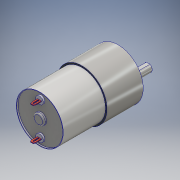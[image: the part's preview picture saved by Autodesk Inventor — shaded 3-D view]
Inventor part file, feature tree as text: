
AUTODESK INVENTOR PART (.ipt)
format: ipt  version: 2016 (Build 200138000, 138)  size: 331,776 bytes
history: native  units: mm
features: extrude x13, sketch x13, chamfer x6, fillet x1, projected_geometry x1
ambient origin geometry x8: Origin, YZ Plane, XZ Plane, XY Plane, X Axis, Y Axis, Z Axis, Center Point
bodies: Solid1 (feature_tree)
feature tree (34):
  extrude  "Extrusion1"  Depth=26.6mm TaperAngle=0.0deg
  extrude  "Extrusion2"  Depth=7.0mm
  chamfer  "Chamfer1"  Distance=6.5mm
  extrude  "Extrusion3"  TaperAngle=0.0deg  [1 undecoded]
  chamfer  "Chamfer3"  Distance=1.0mm
  extrude  "Extrusion4"  Depth=6.0mm
  extrude  "Extrusion5"  Depth=4.3mm
  extrude  "Extrusion6"  Depth=12.0mm
  sketch  "Sketch7"  dims[d16=22.8mm d17=1.0mm d18=0.0mm]
  extrude  "Extrusion7"  Depth=33.8mm
  extrude  "Extrusion8"  Depth=1.0mm
  fillet  "Fillet1"  Radius=2.0mm
  extrude  "Extrusion9"  Depth=12.0mm
  extrude  "Extrusion10"  TaperAngle=0.0deg  [1 undecoded]
  extrude  "Extrusion11"  Depth=12.0mm
  chamfer  "Chamfer4"  Distance=20.0mm Angle=360.0deg
  chamfer  "Chamfer5"  Distance=1.2mm
  extrude  "Extrusion12"  Depth=12.0mm
  chamfer  "Chamfer6"  [1 undecoded]
  chamfer  "Chamfer7"  Distance=3.0mm
  extrude  "Extrusion13"  Depth=12.0mm
  sketch  "Sketch1"  dims[d0=36.8mm d3=26.6mm d4=0.0mm]
  sketch  "Sketch2"  dims[d5=0.0mm d6=7.0mm]
  sketch  "Sketch3"  dims[d7=12.0mm d8=6.5mm d9=0.0mm]
  projected_geometry  "Projected Loop1"
  sketch  "Sketch4"  dims[d10=0.5mm d11=2.0mm d12=45.0deg d13=0.0mm]
  sketch  "Sketch5"  dims[d14=7.0mm]
  sketch  "Sketch6"  dims[d15=17.0mm]
  sketch  "Sketch10"  dims[d22=1.0mm d23=2.0mm d24=45.0deg d25=6.0mm]
  sketch  "Sketch11"  dims[d27=15.5mm d28=0.0mm d33=4.3mm]
  sketch  "Sketch12"  dims[d34=12.0mm d35=0.0mm d36=34.5mm]
  sketch  "Sketch13"  dims[d37=30.0mm d38=0.0mm d39=33.8mm]
  sketch  "Sketch14"  dims[d41=1.0mm d42=0.0mm d43=8.0mm d44=2.0mm d45=0.0mm]
  sketch  "Sketch15"  dims[d46=1.0mm d47=5.5mm d48=0.0mm d49=12.05mm d50=20.0mm d52=360.0deg d54=1.2mm d55=0.0mm d56=12.05mm d57=0.0mm d58=3.0mm d59=0.6mm d60=12.05mm d61=0.0mm d62=0.6mm d63=1.5mm d64=5.6mm d65=0.0mm d66=1.5mm d67=3.0mm d68=1.7mm d69=1.0mm d70=5.6mm d71=0.0mm d72=0.5mm d73=1.0mm d74=45.0deg d75=0.5mm d76=1.0mm d77=45.0deg d78=5.6mm d79=0.0mm d80=0.5mm d81=2.0mm d82=45.0deg d83=0.5mm d84=2.0mm d85=45.0deg d86=3.0mm d87=15.5mm d88=0.0mm d89=60.0mm d91=360.0deg d93=12.0mm d94=0.0mm]
note: 3 required parameter values undecoded (feature->parameter linkage not recoverable at this tier; creation-order binding heuristic only, values carry confidence <= 0.55)
